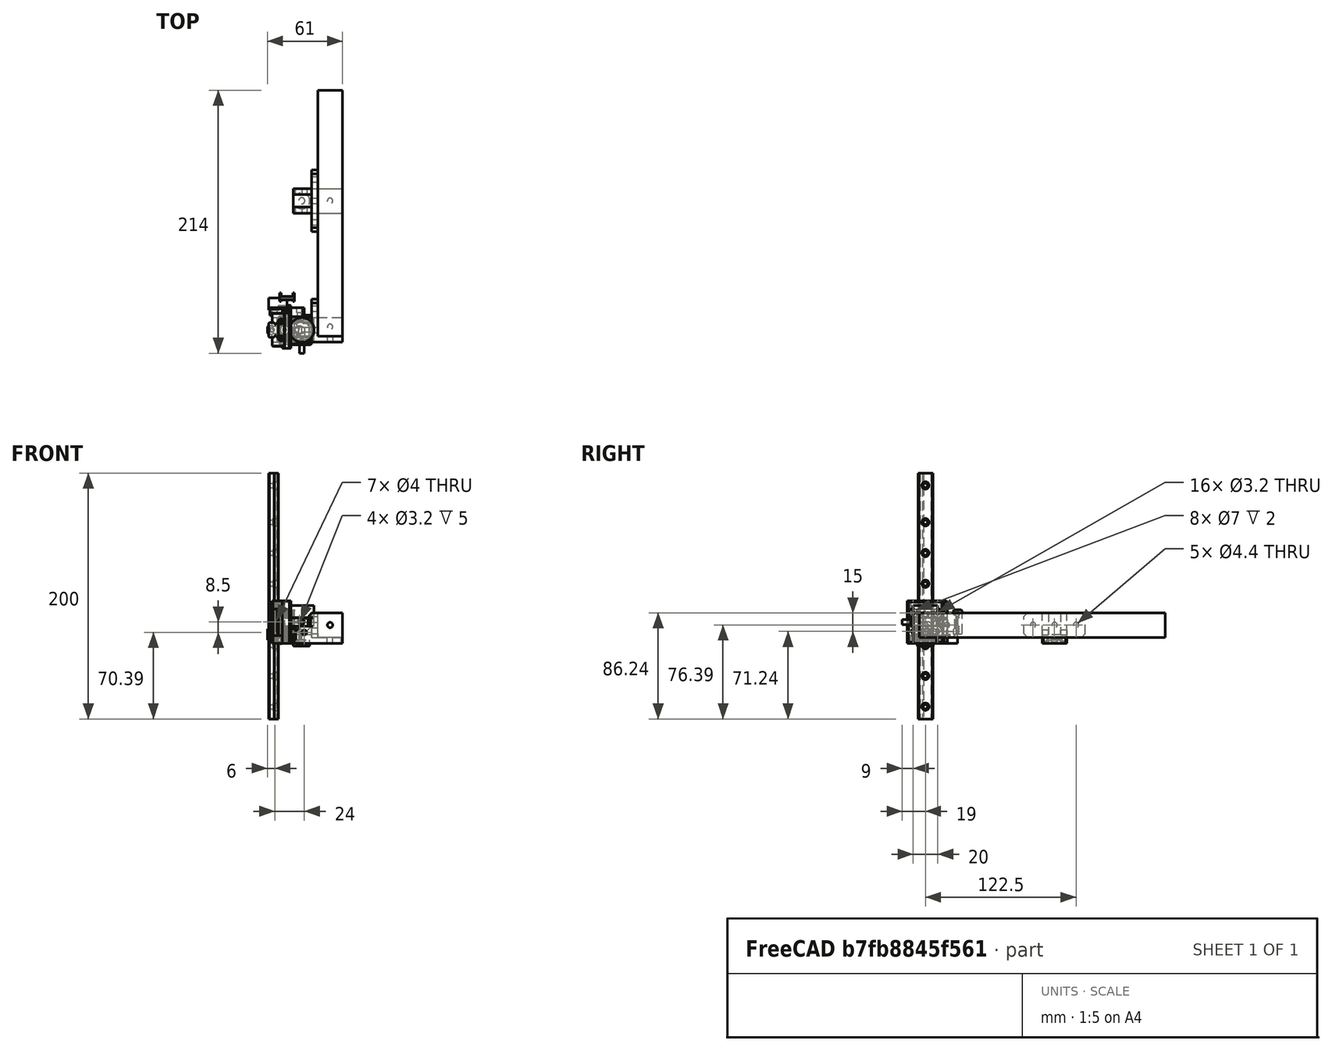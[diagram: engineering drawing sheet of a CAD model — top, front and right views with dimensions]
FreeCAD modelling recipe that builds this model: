
FCSTD DOCUMENT  (FreeCAD 0.18R16146 (Git))
Label: z-rail
License: All rights reserved
LicenseURL: http://en.wikipedia.org/wiki/All_rights_reserved
objects: Part::Box×63, Part::Cylinder×35, Part::MultiFuse×31, Part::Chamfer×29, Part::Cut×24, Part::Feature×16
note: 198 computed .brp shape members not serialized (recipe doc carries the construction recipe); baked Part::Feature solids carry a one-line shape summary decoded from their .brp

FEATURE [Part::Feature] Fusion001001  label="_MGN12-pref"
  Placement = pos=(-7.5,4e-15,38.61) rot=(0,0,-1;1.5708rad)
  shape: bbox 13 x 27 x 200 mm, 427 faces (baked)
FEATURE [Part::Box] Box  label="Cube"
  AttacherType = Attacher::AttachEngine3D
  Height = 34.7
  Length = 5
  Placement = pos=(0,-15,0) rot=(0,0,1;0rad)
  Width = 30
FEATURE [Part::Cylinder] Cylinder
  Angle = 360
  AttacherType = Attacher::AttachEngine3D
  Height = 10
  Placement = pos=(-6e-15,-10,24.85) rot=(0,1,0;1.5708rad)
  Radius = 3.5
FEATURE [Part::Cylinder] Cylinder001
  Angle = 360
  AttacherType = Attacher::AttachEngine3D
  Height = 10
  Placement = pos=(-6e-15,10,24.85) rot=(0,1,0;1.5708rad)
  Radius = 3.5
FEATURE [Part::Cylinder] Cylinder002
  Angle = 360
  AttacherType = Attacher::AttachEngine3D
  Height = 10
  Placement = pos=(-2.2e-15,-10,9.85) rot=(0,1,0;1.5708rad)
  Radius = 3.5
FEATURE [Part::Cylinder] Cylinder003
  Angle = 360
  AttacherType = Attacher::AttachEngine3D
  Height = 10
  Placement = pos=(-2.2e-15,10,9.85) rot=(0,1,0;1.5708rad)
  Radius = 3.5
FEATURE [Part::Cylinder] Cylinder004
  Angle = 360
  AttacherType = Attacher::AttachEngine3D
  Height = 12.3
  Placement = pos=(7.85,5,17) rot=(0,1,0;1.5708rad)
  Radius = 3.1
FEATURE [Part::Cylinder] Cylinder005
  Angle = 360
  AttacherType = Attacher::AttachEngine3D
  Height = 12.3
  Placement = pos=(7.85,-5,17) rot=(0,1,0;1.5708rad)
  Radius = 3.1
FEATURE [Part::Cylinder] Cylinder007
  Angle = 360
  AttacherType = Attacher::AttachEngine3D
  Height = 12.3
  Placement = pos=(9,-6.15,17) rot=(-1,0,0;1.5708rad)
  Radius = 3.1
FEATURE [Part::Cylinder] Cylinder008
  Angle = 360
  AttacherType = Attacher::AttachEngine3D
  Height = 12.3
  Placement = pos=(19,-6.15,17) rot=(-1,0,0;1.5708rad)
  Radius = 3.1
FEATURE [Part::Box] Box001  label="Cube001"
  AttacherType = Attacher::AttachEngine3D
  Height = 34.7
  Length = 5
  Placement = pos=(-2,-15,0) rot=(0,0,1;0rad)
  Width = 1.35
FEATURE [Part::Box] Box002  label="Cube002"
  AttacherType = Attacher::AttachEngine3D
  Height = 34.7
  Length = 5
  Placement = pos=(-2,13.65,0) rot=(0,0,1;0rad)
  Width = 1.35
FEATURE [Part::Box] Box003  label="Cube003"
  AttacherType = Attacher::AttachEngine3D
  Height = 7
  Length = 18
  Placement = pos=(4,-12,11) rot=(0,0,1;0rad)
  Width = 24
FEATURE [Part::MultiFuse] Fusion  label="base-plate"
  Shapes = -> [Box001,Box,Box002]
FEATURE [Part::Cylinder] Cylinder009
  Angle = 360
  AttacherType = Attacher::AttachEngine3D
  Height = 10
  Placement = pos=(14,0,21) rot=(0,0,1;0rad)
  Radius = 10
FEATURE [Part::Feature] Fusion001002  label="base-plate001"
  shape: bbox 7 x 30 x 34.7 mm, 10 faces (baked)
FEATURE [Part::Box] Box004  label="Cube004"
  AttacherType = Attacher::AttachEngine3D
  Height = 7
  Length = 12.3
  Placement = pos=(7.85,-8,15) rot=(0,0,1;0rad)
  Width = 16
FEATURE [Part::Chamfer] Chamfer
  Base = -> Box004
  Edges = 2 edges r=2: [Edge9,Edge11]
FEATURE [Part::Chamfer] Chamfer001
  Base = -> Fusion001002
  Edges = 8 edges r=1: [Edge1,Edge2,Edge3,Edge4,Edge8,Edge10,Edge20,Edge22]
FEATURE [Part::Cylinder] Cylinder010
  Angle = 360
  AttacherType = Attacher::AttachEngine3D
  Height = 10
  Placement = pos=(-6e-15,-10,24.85) rot=(0,1,0;1.5708rad)
  Radius = 1.6
FEATURE [Part::Cylinder] Cylinder011
  Angle = 360
  AttacherType = Attacher::AttachEngine3D
  Height = 10
  Placement = pos=(-6e-15,10,24.85) rot=(0,1,0;1.5708rad)
  Radius = 1.6
FEATURE [Part::Cylinder] Cylinder012
  Angle = 360
  AttacherType = Attacher::AttachEngine3D
  Height = 10
  Placement = pos=(-2.2e-15,10,9.85) rot=(0,1,0;1.5708rad)
  Radius = 1.6
FEATURE [Part::Cylinder] Cylinder013
  Angle = 360
  AttacherType = Attacher::AttachEngine3D
  Height = 10
  Placement = pos=(-2.2e-15,-10,9.85) rot=(0,1,0;1.5708rad)
  Radius = 1.6
FEATURE [Part::MultiFuse] Fusion001004
  Shapes = -> [Cylinder013,Cylinder012,Cylinder011,Cylinder010]
FEATURE [Part::MultiFuse] Fusion001006
  Placement = pos=(3,0,0) rot=(0,0,1;0rad)
  Shapes = -> [Cylinder,Cylinder001]
FEATURE [Part::MultiFuse] Fusion001007
  Placement = pos=(5,0,0) rot=(0,0,1;0rad)
  Shapes = -> [Cylinder002,Cylinder003]
FEATURE [Part::Box] Box005  label="Cube005"
  AttacherType = Attacher::AttachEngine3D
  Height = 15
  Length = 18
  Placement = pos=(4,-6,0) rot=(0,0,1;0rad)
  Width = 4
FEATURE [Part::Box] Box006  label="Cube006"
  AttacherType = Attacher::AttachEngine3D
  Height = 15
  Length = 18
  Placement = pos=(4,2,0) rot=(0,0,1;0rad)
  Width = 4
FEATURE [Part::MultiFuse] Fusion001003
  Shapes = -> [Chamfer,Cylinder005,Cylinder004]
FEATURE [Part::Box] Box007  label="Cube007"
  AttacherType = Attacher::AttachEngine3D
  Height = 7
  Length = 20
  Placement = pos=(4,-12,11) rot=(0,0,1;0rad)
  Width = 24
FEATURE [Part::Feature] Fusion001010  label="base-plate002"
  shape: bbox 7 x 30 x 34.7 mm, 10 faces (baked)
FEATURE [Part::Chamfer] Chamfer005
  Base = -> Fusion001010
  Edges = 8 edges r=1: [Edge1,Edge2,Edge3,Edge4,Edge8,Edge10,Edge20,Edge22]
FEATURE [Part::Feature] Fusion001007001  label="Fusion001009"
  Placement = pos=(5,0,0) rot=(0,0,1;0rad)
  shape: bbox 10 x 27 x 7 mm, 6 faces, 2 solids (baked)
FEATURE [Part::Feature] Fusion001006001  label="Fusion001010"
  Placement = pos=(3,0,0) rot=(0,0,1;0rad)
  shape: bbox 10 x 27 x 7 mm, 6 faces, 2 solids (baked)
FEATURE [Part::Feature] Fusion001004001  label="Fusion001011"
  shape: bbox 10 x 23.2 x 18.2 mm, 12 faces, 4 solids (baked)
FEATURE [Part::Box] Box008  label="Cube008"
  AttacherType = Attacher::AttachEngine3D
  Height = 10
  Length = 16
  Placement = pos=(6,-6.15,15) rot=(0,0,1;0rad)
  Width = 12.3
FEATURE [Part::Chamfer] Chamfer004002
  Base = -> Box008
  Edges = 2 edges r=2: [Edge4,Edge8]
FEATURE [Part::MultiFuse] Fusion001007002
  Shapes = -> [Chamfer004002,Cylinder007,Cylinder008]
FEATURE [Part::Chamfer] Chamfer004003
  Base = -> Box007
  Edges = 2 edges r=3: [Edge5,Edge7]
FEATURE [Part::Cut] Cut004
  Base = -> Chamfer004003
  Tool = -> Fusion001007002
FEATURE [Part::Chamfer] Chamfer004004
  Base = -> Cut004
  Edges = 5 edges r=0.4: [Edge1,Edge5,Edge6,Edge8,Edge9]
  Placement = pos=(0,0,3) rot=(0,0,1;0rad)
FEATURE [Part::Chamfer] Chamfer004006
  Base = -> Box003
  Edges = 2 edges r=3: [Edge5,Edge7]
FEATURE [Part::Chamfer] Chamfer004007
  Base = -> Chamfer004006
  Edges = 5 edges r=0.4: [Edge1,Edge5,Edge6,Edge8,Edge9]
FEATURE [Part::Cut] Cut
  Base = -> Chamfer004007
  Placement = pos=(0,0,3) rot=(0,0,1;0rad)
  Tool = -> Fusion001003
FEATURE [Part::Cylinder] Cylinder014
  Angle = 360
  AttacherType = Attacher::AttachEngine3D
  Height = 5
  Placement = pos=(14,0,0) rot=(0,0,1;0rad)
  Radius = 6.5
FEATURE [Part::Cylinder] Cylinder015
  Angle = 360
  AttacherType = Attacher::AttachEngine3D
  Height = 2
  Placement = pos=(14,0,3) rot=(0,0,1;0rad)
  Radius = 2.5
FEATURE [Part::Box] Box009  label="Cube009"
  AttacherType = Attacher::AttachEngine3D
  Height = 7
  Length = 20
  Placement = pos=(7,-10,0) rot=(0,0,1;0rad)
  Width = 20
FEATURE [Part::Box] Box010  label="Cube010"
  AttacherType = Attacher::AttachEngine3D
  Height = 5
  Length = 4
  Placement = pos=(7,-5,0) rot=(0,0,1;0rad)
  Width = 10
FEATURE [Part::Cut] Cut011
  Base = -> Cylinder014
  Tool = -> Cylinder015
FEATURE [Part::Box] Box011  label="2020"
  AttacherType = Attacher::AttachEngine3D
  Height = 20
  Length = 20
  Placement = pos=(27,-5,5) rot=(0,0,1;0rad)
  Width = 200
FEATURE [Part::MultiFuse] Fusion001007005  label="magnet-slot"
  Placement = pos=(0,0,-2) rot=(0,0,1;0rad)
  Shapes = -> [Cut011,Box010]
FEATURE [Part::Box] Box012  label="Cube011"
  AttacherType = Attacher::AttachEngine3D
  Height = 5
  Length = 20
  Placement = pos=(27,-10,0) rot=(0,0,1;0rad)
  Width = 20
FEATURE [Part::Box] Box013  label="Cube012"
  AttacherType = Attacher::AttachEngine3D
  Height = 25
  Length = 20
  Placement = pos=(27,-10,0) rot=(0,0,1;0rad)
  Width = 5
FEATURE [Part::Box] Box014  label="Cube013"
  AttacherType = Attacher::AttachEngine3D
  Height = 25
  Length = 5
  Placement = pos=(22,-10,0) rot=(0,0,1;0rad)
  Width = 20
FEATURE [Part::Box] Box015  label="Cube014"
  AttacherType = Attacher::AttachEngine3D
  Height = 19
  Length = 16
  Placement = pos=(7,-10,6) rot=(0,0,1;0rad)
  Width = 5
FEATURE [Part::Box] Box016  label="Cube015"
  AttacherType = Attacher::AttachEngine3D
  Height = 19
  Length = 16
  Placement = pos=(7,5,6) rot=(0,0,1;0rad)
  Width = 5
FEATURE [Part::Feature] Fusion001007005001  label="magnet-slot001"
  Placement = pos=(0,105,-2) rot=(0,0,1;0rad)
  shape: bbox 13.5 x 13 x 5 mm, 13 faces (baked)
FEATURE [Part::Box] Box017  label="Cube016"
  AttacherType = Attacher::AttachEngine3D
  Height = 20
  Length = 5
  Placement = pos=(22,9,5) rot=(0,0,1;0rad)
  Width = 16
FEATURE [Part::MultiFuse] Fusion001007005002
  Shapes = -> [Box016,Box015]
FEATURE [Part::Chamfer] Chamfer004009
  Base = -> Fusion001007005002
  Edges = 2 edges: [Edge2 r1=18 r2=15,Edge14 r1=18 r2=15]
FEATURE [Part::Chamfer] Chamfer004010
  Base = -> Box017
  Edges = 2 edges r=3: [Edge11,Edge12]
FEATURE [Part::Chamfer] Chamfer004011
  Base = -> Box012
  Edges = 1 edges r=1: [Edge7]
FEATURE [Part::Feature] Fusion001007005003  label="magnet-slot002"
  Placement = pos=(0,0,-2) rot=(0,0,1;0rad)
  shape: bbox 13.5 x 13 x 5 mm, 13 faces (baked)
FEATURE [Part::Cut] Cut012
  Base = -> Box009
  Tool = -> Fusion001007005003
FEATURE [Part::Chamfer] Chamfer004012
  Base = -> Cut012
  Edges = 2 edges r=2: [Edge3,Edge7]
FEATURE [Part::MultiFuse] Fusion001007005004
  Shapes = -> [Chamfer004012,Chamfer004011,Chamfer004010,Chamfer004009,Box014,Box013]
FEATURE [Part::Cylinder] Cylinder016
  Angle = 360
  AttacherType = Attacher::AttachEngine3D
  Height = 10
  Placement = pos=(37,2.5,-3) rot=(0,0,1;0rad)
  Radius = 2.2
FEATURE [Part::Cylinder] Cylinder017
  Angle = 360
  AttacherType = Attacher::AttachEngine3D
  Height = 10
  Placement = pos=(37,-2.5,15) rot=(1,0,0;1.5708rad)
  Radius = 2.2
FEATURE [Part::Cylinder] Cylinder018
  Angle = 360
  AttacherType = Attacher::AttachEngine3D
  Height = 10
  Placement = pos=(18,0,15) rot=(0,1,0;1.5708rad)
  Radius = 2.2
FEATURE [Part::Cylinder] Cylinder019
  Angle = 360
  AttacherType = Attacher::AttachEngine3D
  Height = 10
  Placement = pos=(18,17.5,15) rot=(0,1,0;1.5708rad)
  Radius = 2.2
FEATURE [Part::MultiFuse] Fusion001007005005
  Shapes = -> [Cylinder019,Cylinder018,Cylinder017,Cylinder016]
FEATURE [Part::MultiFuse] Fusion001007005006
  Shapes = -> [Box005,Box006]
FEATURE [Part::Chamfer] Chamfer004013
  Base = -> Fusion001007005006
  Edges = 2 edges r=14: [Edge8,Edge20]
FEATURE [Part::MultiFuse] Fusion001007005007
  Shapes = -> [Chamfer001,Cut,Chamfer004013]
FEATURE [Part::MultiFuse] Fusion001007005008
  Shapes = -> [Fusion001004,Fusion001006,Fusion001007]
FEATURE [Part::Cut] Cut014  label="slider-x"
  Base = -> Fusion001007005007
  Tool = -> Fusion001007005008
FEATURE [Part::MultiFuse] Fusion001007005009
  Shapes = -> [Fusion001004001,Fusion001006001,Fusion001007001]
FEATURE [Part::Feature] Chamfer004013001  label="Chamfer004014"
  shape: bbox 18 x 12 x 15 mm, 14 faces, 2 solids (baked)
FEATURE [Part::MultiFuse] Fusion001007005010
  Shapes = -> [Chamfer004004,Chamfer005,Chamfer004013001]
FEATURE [Part::Cut] Cut015  label="slider-y"
  Base = -> Fusion001007005010
  Tool = -> Fusion001007005009
FEATURE [Part::Cylinder] Cylinder020
  Angle = 360
  AttacherType = Attacher::AttachEngine3D
  Height = 10
  Placement = pos=(14,-9,17.5) rot=(1,0,0;1.5708rad)
  Radius = 2
FEATURE [Part::Cylinder] Cylinder021
  Angle = 360
  AttacherType = Attacher::AttachEngine3D
  Height = 10
  Placement = pos=(14,-9,17.5) rot=(1,0,0;1.5708rad)
  Radius = 2
FEATURE [Part::Cylinder] Cylinder022
  Angle = 360
  AttacherType = Attacher::AttachEngine3D
  Height = 10
  Placement = pos=(14,-9,17.5) rot=(1,0,0;1.5708rad)
  Radius = 2
FEATURE [Part::Cut] Cut016  label="slider-x001"
  Base = -> Cut014
  Tool = -> Cylinder022
FEATURE [Part::Cut] Cut017  label="slider-y001"
  Base = -> Cut015
  Tool = -> Cylinder021
FEATURE [Part::Box] Box018  label="Cube017"
  AttacherType = Attacher::AttachEngine3D
  Height = 10
  Length = 15
  Placement = pos=(-13,16,0) rot=(0,0,1;0rad)
  Width = 10
FEATURE [Part::Box] Box019  label="Cube018"
  AttacherType = Attacher::AttachEngine3D
  Height = 1.3
  Length = 6.5
  Placement = pos=(-3.25,2,0) rot=(0,0,1;0rad)
  Width = 1.2
FEATURE [Part::Box] Box020  label="Cube019"
  AttacherType = Attacher::AttachEngine3D
  Height = 1.3
  Length = 6.5
  Placement = pos=(-3.25,4,0) rot=(0,0,1;0rad)
  Width = 1.2
FEATURE [Part::Box] Box021  label="Cube020"
  AttacherType = Attacher::AttachEngine3D
  Height = 1.3
  Length = 6.5
  Placement = pos=(-3.25,6,0) rot=(0,0,1;0rad)
  Width = 1.2
FEATURE [Part::Box] Box022  label="Cube021"
  AttacherType = Attacher::AttachEngine3D
  Height = 1.3
  Length = 6.5
  Placement = pos=(-3.25,8,0) rot=(0,0,1;0rad)
  Width = 1.2
FEATURE [Part::Box] Box023  label="main-btlt-hld"
  AttacherType = Attacher::AttachEngine3D
  Height = 6
  Length = 12
  Placement = pos=(-6,-10,0) rot=(0,0,1;0rad)
  Width = 20
FEATURE [Part::Box] Box024  label="Cube023"
  AttacherType = Attacher::AttachEngine3D
  Height = 1.3
  Length = 6.5
  Placement = pos=(-3.25,-3.2,0) rot=(0,0,1;0rad)
  Width = 1.2
FEATURE [Part::Box] Box025  label="Cube024"
  AttacherType = Attacher::AttachEngine3D
  Height = 1.3
  Length = 6.5
  Placement = pos=(-3.25,-5.2,0) rot=(0,0,1;0rad)
  Width = 1.2
FEATURE [Part::Box] Box026  label="Cube025"
  AttacherType = Attacher::AttachEngine3D
  Height = 1.3
  Length = 6.5
  Placement = pos=(-3.25,-7.2,0) rot=(0,0,1;0rad)
  Width = 1.2
FEATURE [Part::Box] Box027  label="Cube026"
  AttacherType = Attacher::AttachEngine3D
  Height = 1.3
  Length = 6.5
  Placement = pos=(-3.25,-9.2,0) rot=(0,0,1;0rad)
  Width = 1.2
FEATURE [Part::Box] Box028  label="Cube027"
  AttacherType = Attacher::AttachEngine3D
  Height = 3.5
  Length = 6.5
  Placement = pos=(-3.25,-9.2,0) rot=(0,0,1;0rad)
  Width = 1.2
FEATURE [Part::Box] Box029  label="Cube028"
  AttacherType = Attacher::AttachEngine3D
  Height = 3.5
  Length = 6.5
  Placement = pos=(-3.25,-7.2,0) rot=(0,0,1;0rad)
  Width = 1.2
FEATURE [Part::Box] Box030  label="Cube029"
  AttacherType = Attacher::AttachEngine3D
  Height = 3.5
  Length = 6.5
  Placement = pos=(-3.25,-5.2,0) rot=(0,0,1;0rad)
  Width = 1.2
FEATURE [Part::Box] Box031  label="Cube030"
  AttacherType = Attacher::AttachEngine3D
  Height = 3.5
  Length = 6.5
  Placement = pos=(-3.25,-3.2,0) rot=(0,0,1;0rad)
  Width = 5.2
FEATURE [Part::Box] Box032  label="Cube031"
  AttacherType = Attacher::AttachEngine3D
  Height = 3.5
  Length = 6.5
  Placement = pos=(-3.25,8,0) rot=(0,0,1;0rad)
  Width = 1.2
FEATURE [Part::Box] Box033  label="Cube032"
  AttacherType = Attacher::AttachEngine3D
  Height = 3.5
  Length = 6.5
  Placement = pos=(-3.25,6,0) rot=(0,0,1;0rad)
  Width = 1.2
FEATURE [Part::Box] Box034  label="Cube033"
  AttacherType = Attacher::AttachEngine3D
  Height = 3.5
  Length = 6.5
  Placement = pos=(-3.25,4,0) rot=(0,0,1;0rad)
  Width = 1.2
FEATURE [Part::Box] Box035  label="Cube034"
  AttacherType = Attacher::AttachEngine3D
  Height = 3.5
  Length = 6.5
  Placement = pos=(-3.25,2,0) rot=(0,0,1;0rad)
  Width = 1.2
FEATURE [Part::MultiFuse] Fusion001007005011
  Shapes = -> [Box033,Box034,Box032,Box031,Box035,Box030,Box029,Box028]
FEATURE [Part::Cut] Cut018
  Base = -> Box023
  Tool = -> Fusion001007005011
FEATURE [Part::Box] Box036  label="Cube035"
  AttacherType = Attacher::AttachEngine3D
  Height = 2.2
  Length = 6.5
  Placement = pos=(-3.25,-10,0) rot=(0,0,1;0rad)
  Width = 20
FEATURE [Part::Cut] Cut019
  Base = -> Cut018
  Tool = -> Box036
FEATURE [Part::Box] Box037  label="Cube036"
  AttacherType = Attacher::AttachEngine3D
  Height = 10
  Length = 6.5
  Placement = pos=(-3.25,-3.2,0) rot=(0,0,1;0rad)
  Width = 6.4
FEATURE [Part::MultiFuse] Fusion001007005012
  Placement = pos=(0,0,4.7) rot=(0,0,1;0rad)
  Shapes = -> [Box027,Box019,Box025,Box024,Box026,Box021,Box022,Box020]
FEATURE [Part::Cut] Cut020
  Base = -> Cut019
  Tool = -> Fusion001007005012
FEATURE [Part::Box] Box038  label="Cube037"
  AttacherType = Attacher::AttachEngine3D
  Height = 0.5
  Length = 6.5
  Placement = pos=(-3.25,-10,2.2) rot=(0,0,1;0rad)
  Width = 20
FEATURE [Part::Box] Box039  label="Cube038"
  AttacherType = Attacher::AttachEngine3D
  Height = 0.5
  Length = 6.5
  Placement = pos=(-3.25,-10,5.5) rot=(0,0,1;0rad)
  Width = 20
FEATURE [Part::Box] Box040  label="Cube039"
  AttacherType = Attacher::AttachEngine3D
  Height = 2
  Length = 2.75
  Placement = pos=(-6,-10,5) rot=(0,0,1;0rad)
  Width = 4.9
FEATURE [Part::Box] Box041  label="Cube040"
  AttacherType = Attacher::AttachEngine3D
  Height = 2
  Length = 2.75
  Placement = pos=(3.25,-10,5) rot=(0,0,1;0rad)
  Width = 4.9
FEATURE [Part::Box] Box042  label="Cube041"
  AttacherType = Attacher::AttachEngine3D
  Height = 2
  Length = 2.75
  Placement = pos=(3.25,5.1,5) rot=(0,0,1;0rad)
  Width = 4.9
FEATURE [Part::Box] Box043  label="Cube042"
  AttacherType = Attacher::AttachEngine3D
  Height = 2
  Length = 2.75
  Placement = pos=(-6,5.1,5) rot=(0,0,1;0rad)
  Width = 4.9
FEATURE [Part::MultiFuse] Fusion001007005013
  Shapes = -> [Box040,Box041,Box042,Box043]
FEATURE [Part::Chamfer] Chamfer004013002
  Base = -> Fusion001007005013
  Edges = 4 edges r=1: [Edge12,Edge24,Edge34,Edge46]
FEATURE [Part::Box] Box044  label="Cube043"
  AttacherType = Attacher::AttachEngine3D
  Height = 7
  Length = 12.3
  Placement = pos=(-6.15,-10,0) rot=(0,0,1;0rad)
  Width = 20
FEATURE [Part::Cylinder] Cylinder023
  Angle = 360
  AttacherType = Attacher::AttachEngine3D
  Height = 18
  Radius = 1.65
FEATURE [Part::Cylinder] Cylinder024
  Angle = 360
  AttacherType = Attacher::AttachEngine3D
  Height = 18
  Placement = pos=(-10,0,0) rot=(0,0,1;0rad)
  Radius = 1.65
FEATURE [Part::Cylinder] Cylinder025
  Angle = 360
  AttacherType = Attacher::AttachEngine3D
  Height = 18
  Placement = pos=(10,0,0) rot=(0,0,1;0rad)
  Radius = 1.65
FEATURE [Part::Box] Box045  label="Cube044"
  AttacherType = Attacher::AttachEngine3D
  Height = 9
  Length = 20
  Placement = pos=(-10,-10,3) rot=(0,0,1;0rad)
  Width = 20
FEATURE [Part::Box] Box046  label="Cube045"
  AttacherType = Attacher::AttachEngine3D
  Height = 9
  Length = 28
  Placement = pos=(-14,-3.5,3) rot=(0,0,1;0rad)
  Width = 7
FEATURE [Part::Box] Box047  label="Cube046"
  AttacherType = Attacher::AttachEngine3D
  Height = 7
  Length = 12.3
  Placement = pos=(-6.15,-10,0) rot=(0,0,1;0rad)
  Width = 20
FEATURE [Part::Cut] Cut024
  Base = -> Box045
  Tool = -> Box047
FEATURE [Part::Cylinder] Cylinder026
  Angle = 360
  AttacherType = Attacher::AttachEngine3D
  Height = 2
  Placement = pos=(0,0,10) rot=(0,0,1;0rad)
  Radius = 3.5
FEATURE [Part::MultiFuse] Fusion001007005014
  Shapes = -> [Cylinder024,Cylinder025,Cylinder023]
FEATURE [Part::Box] Box048  label="Cube047"
  AttacherType = Attacher::AttachEngine3D
  Height = 10
  Length = 3.05
  Placement = pos=(-6.15,-10,0) rot=(0,0,1;0rad)
  Width = 5
FEATURE [Part::Box] Box049  label="Cube048"
  AttacherType = Attacher::AttachEngine3D
  Height = 10
  Length = 3.05
  Placement = pos=(3.1,-10,0) rot=(0,0,1;0rad)
  Width = 5
FEATURE [Part::Box] Box050  label="Cube049"
  AttacherType = Attacher::AttachEngine3D
  Height = 10
  Length = 3.05
  Placement = pos=(3.1,5,0) rot=(0,0,1;0rad)
  Width = 5
FEATURE [Part::Box] Box051  label="Cube050"
  AttacherType = Attacher::AttachEngine3D
  Height = 10
  Length = 3.05
  Placement = pos=(-6.15,5,0) rot=(0,0,1;0rad)
  Width = 5
FEATURE [Part::MultiFuse] Fusion001007005016
  Shapes = -> [Box048,Box049,Box050,Box051]
FEATURE [Part::Chamfer] Chamfer004013004
  Base = -> Fusion001007005016
  Edges = 4 edges r=1: [Edge12,Edge24,Edge34,Edge46]
  Placement = pos=(0,0,-2) rot=(0,0,1;0rad)
FEATURE [Part::Cut] Cut029
  Base = -> Cut020
  Tool = -> Box037
FEATURE [Part::MultiFuse] Fusion001007005017
  Shapes = -> [Box038,Box039]
FEATURE [Part::Cut] Cut030
  Base = -> Cut029
  Tool = -> Fusion001007005017
FEATURE [Part::MultiFuse] Fusion001007005018
  Shapes = -> [Cut030,Chamfer004013002]
FEATURE [Part::Chamfer] Chamfer004013005
  Base = -> Fusion001007005018
  Edges = 4 edges r=0.4: [Edge250,Edge261,Edge457,Edge458]
FEATURE [Part::Chamfer] Chamfer004013006  label="belt-holder"
  Base = -> Chamfer004013005
  Edges = 4 edges r=1: [Edge146,Edge152,Edge161,Edge167]
FEATURE [Part::Cut] Cut028002
  Base = -> Box046
  Tool = -> Box044
FEATURE [Part::MultiFuse] Fusion001007005019
  Shapes = -> [Cut024,Cut028002]
FEATURE [Part::Cut] Cut028003
  Base = -> Fusion001007005019
  Tool = -> Chamfer004013004
FEATURE [Part::MultiFuse] Fusion001007005020
  Shapes = -> [Fusion001007005014,Cylinder026]
FEATURE [Part::Cut] Cut028004
  Base = -> Cut028003
  Tool = -> Fusion001007005020
FEATURE [Part::Chamfer] Chamfer004013007  label="belt-connector"
  Base = -> Cut028004
  Edges = 8 edges r=1: [Edge4,Edge11,Edge26,Edge49,Edge95,Edge111,Edge122,Edge127]
FEATURE [Part::Box] Box052  label="Cube051"
  AttacherType = Attacher::AttachEngine3D
  Height = 7
  Length = 11
  Placement = pos=(5,10.65,14) rot=(0,0,1;0rad)
  Width = 7.35
FEATURE [Part::Box] Box053  label="Cube052"
  AttacherType = Attacher::AttachEngine3D
  Height = 34.7
  Length = 17
  Placement = pos=(-12,13.65,0) rot=(0,0,1;0rad)
  Width = 4.35
FEATURE [Part::Chamfer] Chamfer004013007002
  Base = -> Box052
  Edges = 2 edges r=1: [Edge6,Edge8]
FEATURE [Part::Chamfer] Chamfer004013007003
  Base = -> Box053
  Edges = 2 edges r=10: [Edge2,Edge4]
FEATURE [Part::Chamfer] Chamfer004013007004
  Base = -> Chamfer004013007003
  Edges = 6 edges r=1: [Edge11,Edge13,Edge14,Edge16,Edge17,Edge18]
FEATURE [Part::Box] Box054  label="Cube053"
  AttacherType = Attacher::AttachEngine3D
  Height = 12.7
  Length = 1.85
  Placement = pos=(-12,11.65,11) rot=(0,0,1;0rad)
  Width = 3
FEATURE [Part::Chamfer] Chamfer004013007005
  Base = -> Box054
  Edges = 2 edges r=2: [Edge9,Edge10]
FEATURE [Part::Box] Box055  label="Cube054"
  AttacherType = Attacher::AttachEngine3D
  Height = 3
  Length = 10
  Placement = pos=(-5,17,4.5) rot=(0,0,1;0rad)
  Width = 3
FEATURE [Part::Chamfer] Chamfer004013007006
  Base = -> Box055
  Edges = 1 edges r=2: [Edge11]
FEATURE [Part::Chamfer] Chamfer004013007007
  Base = -> Chamfer004013007006
  Edges = 4 edges r=0.4: [Edge1,Edge2,Edge6,Edge10]
FEATURE [Part::MultiFuse] Fusion001007005021  label="belt-side-mount"
  Shapes = -> [Chamfer004013007007,Chamfer004013007005,Chamfer004013007004,Chamfer004013007002]
FEATURE [Part::Cylinder] Cylinder027
  Angle = 360
  AttacherType = Attacher::AttachEngine3D
  Height = 10
  Placement = pos=(-8,13.5,17.5) rot=(-1,0,0;1.5708rad)
  Radius = 2
FEATURE [Part::Cylinder] Cylinder028
  Angle = 360
  AttacherType = Attacher::AttachEngine3D
  Height = 4
  Placement = pos=(12,14,17.5) rot=(-1,0,0;1.5708rad)
  Radius = 2
FEATURE [Part::Cylinder] Cylinder029
  Angle = 360
  AttacherType = Attacher::AttachEngine3D
  Height = 10
  Placement = pos=(12,9,17.5) rot=(-1,0,0;1.5708rad)
  Radius = 1.6
FEATURE [Part::MultiFuse] Fusion001007005022
  Shapes = -> [Cylinder029,Cylinder028,Cylinder027]
FEATURE [Part::Feature] Fusion001007005021001  label="belt-side-mount001"
  shape: bbox 28 x 9.35 x 34.7 mm, 39 faces (baked)
FEATURE [Part::Feature] Fusion001007005021002  label="belt-side-mount002"
  shape: bbox 28 x 9.35 x 34.7 mm, 39 faces (baked)
FEATURE [Part::Feature] Fusion001007005022001  label="Fusion001007005023"
  shape: bbox 24 x 14.5 x 4 mm, 10 faces, 2 solids (baked)
FEATURE [Part::MultiFuse] Fusion001007005022002
  Shapes = -> [Fusion001007005021002,Cut016]
FEATURE [Part::Cut] Cut028005  label="x-slider"
  Base = -> Fusion001007005022002
  Tool = -> Fusion001007005022001
FEATURE [Part::MultiFuse] Fusion001007005022003
  Shapes = -> [Cut017,Fusion001007005021001]
FEATURE [Part::Cut] Cut028006  label="y-slider"
  Base = -> Fusion001007005022003
  Tool = -> Fusion001007005022
FEATURE [Part::Box] Box056  label="Cube055"
  AttacherType = Attacher::AttachEngine3D
  Height = 5
  Length = 40
  Placement = pos=(7,95,0) rot=(0,0,1;0rad)
  Width = 20
FEATURE [Part::Cut] Cut028007
  Base = -> Box056
  Tool = -> Fusion001007005001
FEATURE [Part::Box] Box057  label="Cube056"
  AttacherType = Attacher::AttachEngine3D
  Height = 2
  Length = 20
  Placement = pos=(7,95,5) rot=(0,0,1;0rad)
  Width = 20
FEATURE [Part::Box] Box058  label="Cube057"
  AttacherType = Attacher::AttachEngine3D
  Height = 20
  Length = 5
  Placement = pos=(22,95,5) rot=(0,0,1;0rad)
  Width = 20
FEATURE [Part::Box] Box059  label="Cube058"
  AttacherType = Attacher::AttachEngine3D
  Height = 20
  Length = 5
  Placement = pos=(22,80,5) rot=(0,0,1;0rad)
  Width = 15
FEATURE [Part::Box] Box060  label="Cube059"
  AttacherType = Attacher::AttachEngine3D
  Height = 20
  Length = 5
  Placement = pos=(22,115,5) rot=(0,0,1;0rad)
  Width = 15
FEATURE [Part::Box] Box061  label="Cube060"
  AttacherType = Attacher::AttachEngine3D
  Height = 19
  Length = 16
  Placement = pos=(7,95,6) rot=(0,0,1;0rad)
  Width = 5
FEATURE [Part::Box] Box062  label="Cube061"
  AttacherType = Attacher::AttachEngine3D
  Height = 19
  Length = 16
  Placement = pos=(7,110,6) rot=(0,0,1;0rad)
  Width = 5
FEATURE [Part::Chamfer] Chamfer004013007008
  Base = -> Cut028007
  Edges = 2 edges r=2: [Edge3,Edge7]
FEATURE [Part::MultiFuse] Fusion001007005022004
  Shapes = -> [Box062,Box061]
FEATURE [Part::Chamfer] Chamfer004013007009
  Base = -> Fusion001007005022004
  Edges = 2 edges: [Edge2 r1=18 r2=15,Edge14 r1=18 r2=15]
FEATURE [Part::Chamfer] Chamfer004013007010
  Base = -> Chamfer004013007008
  Edges = 2 edges r=1: [Edge11,Edge22]
FEATURE [Part::Chamfer] Chamfer004013007011
  Base = -> Box060
  Edges = 2 edges r=3: [Edge11,Edge12]
FEATURE [Part::Chamfer] Chamfer004013007012
  Base = -> Box059
  Edges = 2 edges r=3: [Edge9,Edge10]
FEATURE [Part::MultiFuse] Fusion001007005022005
  Shapes = -> [Chamfer004013007012,Chamfer004013007011,Chamfer004013007010,Chamfer004013007009,Box058,Box057]
FEATURE [Part::Cylinder] Cylinder030
  Angle = 360
  AttacherType = Attacher::AttachEngine3D
  Height = 10
  Placement = pos=(18,105,15) rot=(0,1,0;1.5708rad)
  Radius = 2.2
FEATURE [Part::Cylinder] Cylinder031
  Angle = 360
  AttacherType = Attacher::AttachEngine3D
  Height = 10
  Placement = pos=(18,122.5,15) rot=(0,1,0;1.5708rad)
  Radius = 2.2
FEATURE [Part::Cylinder] Cylinder033
  Angle = 360
  AttacherType = Attacher::AttachEngine3D
  Height = 10
  Placement = pos=(37,105,-3) rot=(0,0,1;0rad)
  Radius = 2.2
FEATURE [Part::Cylinder] Cylinder034
  Angle = 360
  AttacherType = Attacher::AttachEngine3D
  Height = 10
  Placement = pos=(18,87.5,15) rot=(0,1,0;1.5708rad)
  Radius = 2.2
FEATURE [Part::MultiFuse] Fusion001007005022006
  Shapes = -> [Cylinder034,Cylinder033,Cylinder031,Cylinder030]
FEATURE [Part::Cut] Cut028008
  Base = -> Fusion001007005022005
  Tool = -> Fusion001007005022006
FEATURE [Part::Cylinder] Cylinder035
  Angle = 360
  AttacherType = Attacher::AttachEngine3D
  Height = 10
  Placement = pos=(16,-4,9) rot=(1,0,0;1.5708rad)
  Radius = 2
FEATURE [Part::Cylinder] Cylinder036
  Angle = 360
  AttacherType = Attacher::AttachEngine3D
  Height = 26
  Placement = pos=(16,118,9) rot=(1,0,0;1.5708rad)
  Radius = 2
FEATURE [Part::Cut] Cut028009
  Base = -> Cut028008
  Tool = -> Cylinder036
FEATURE [Part::Cut] Cut028010
  Base = -> Fusion001007005004
  Tool = -> Fusion001007005005
FEATURE [Part::Cut] Cut028011
  Base = -> Cut028010
  Tool = -> Cylinder035
FEATURE [Part::Feature] Cut028006001  label="y-slider001"
  shape: bbox 36 x 35 x 34.7 mm, 80 faces (baked)
FEATURE [Part::Feature] Cut028005001  label="x-slider001"
  shape: bbox 34 x 35 x 34.7 mm, 82 faces (baked)
FEATURE [Part::Feature] Fusion003001  label="belt-mounter-9mm001"
  Placement = pos=(2,30,17.5) rot=(1,0,0;1.5708rad)
  shape: bbox 12 x 7 x 20 mm, 88 faces (baked)
FEATURE [Part::Feature] Fusion004001  label="belt-holder-9mm001"
  shape: bbox 28 x 20 x 9 mm, 43 faces (baked)
